# Revit family: Shower-Valve_Trim-KOHLER-Recessed-K-26476T
name_source: partatom
category: Specialty Equipment
units: mm (PartAtom-declared; Revit-internal decimal feet)

## family parameters
Cut with Voids When Loaded = No
Host = Face
Maintain Annotation Orientation = No
OmniClass Number = 23.31.25.00
OmniClass Title = Toilet and Bath Specialties
Part Type = Normal
Room Calculation Point = No
Round Connector Dimension = Use Diameter
Shared = No

## types (10) — shared parameters
ADA Compliant = No
Assembly Code = C1030200
Date Modified = 01/09/2025
Default Elevation = 42"
Description = 40MM In-Wall Bathtub Shower Panel Modern Round
Handle clearance = 3 3/16"
Height = 6 5/16"
Length = 3"
Manufacturer = Kohler Co.
Master Format 2014 = 10 28 00
Master Format 2014 Name = Toilet, Bath, and Laundry Accessories
Material = Premium Metal Construction
Product Documentation Link = https://files.kohler.com.cn
Product Name = Recessed
URL = http://www.kohler.com.cn
WaterSense Certified = No
Width = 6 5/16"

## per-type parameters (varying)
| type | Finish | Model | Product Page URL | Type |
| 2BL-Black | KOHLER-Metal-2BL-Black | K-26476T-4-2BL |  | 1 |
| 2MB-Vibrant Brushed Moderne Brass | Kohler-Metal-2MB-Vibrant_Brushed_Moderne_Brass | K-26476T-4-2MB |  | 2 |
| AF-Vibrant French Gold | Kohler-Metal-AF-Vibrant_French_Gold | K-26476T-4-AF |  | 3 |
| BL-Matte Black | Kohler-Metal-BL-Matte_Black | K-26476T-4-BL |  | 4 |
| BN-Vibrant Brushed Nickel | Kohler-Metal-BN-Vibrant_Brushed_Nickel | K-26476T-4-BN |  | 5 |
| BV-Brushed Bronze | Kohler-Metal-BV-Brushed_Bronze | K-26476T-4-BV |  | 6 |
| CP-Polished Chrome | Kohler-Metal-CP-Polished_Chrome | K-26476T-4-CP | https://www.kohler.com.cn | 7 |
| RGD-Polished Rose Gold | Kohler-Metal-RGD-Polished_Rose_Gold | K-26476T-4-RGD |  | 8 |
| SN-Vibrant Polished Nickel | Kohler-Metal-SN-Vibrant_Polished_Nickel | K-26476T-4-SN |  | 9 |
| LBN-Non Pvd Brushed Nickel | Kohler-Metal-LBN-Non_Pvd_Brushed_Nickel | K-26476T-4-LBN |  | 10 |

## geometry (parser evidence)
native form markers: Sweep x4
no freeform markers — native parametric forms only
